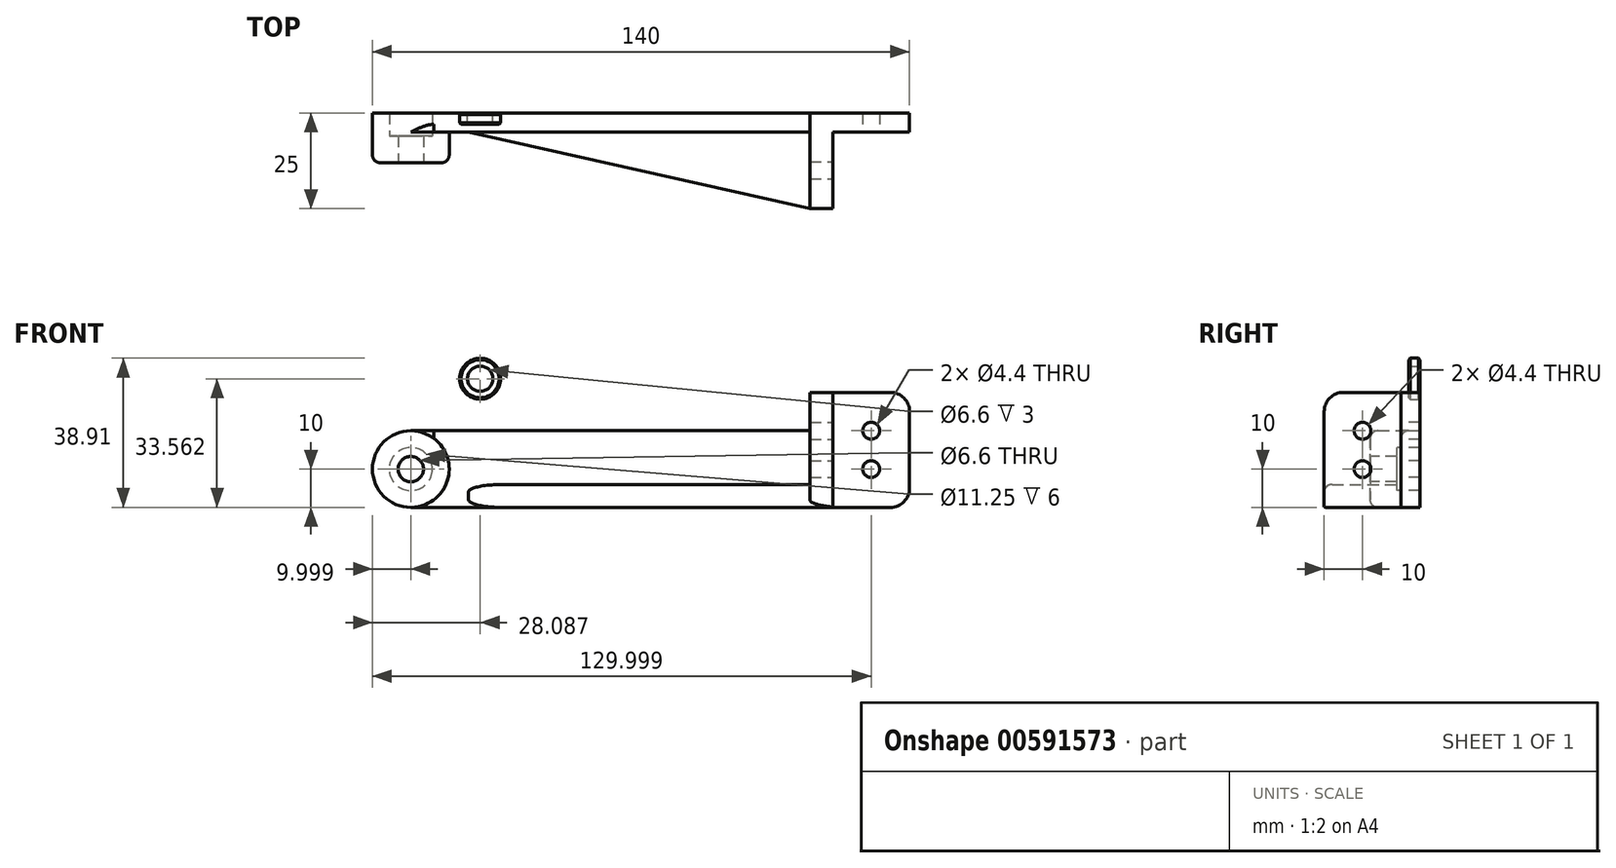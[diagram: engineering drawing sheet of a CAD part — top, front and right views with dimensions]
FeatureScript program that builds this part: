
annotation { "Feature Type Name" : "Feature", "Feature Type Description" : "" }
export const myFeature = defineFeature(function(context is Context, id is Id, definition is map)
    precondition{}
    {
        {
            var Q0;
            Q0=qCreatedBy(makeId("Top.planeOp"),FACE);
            var sketch = newSketch(context, id + "F0", { "sketchPlane" : qUnion([Q0])});
            skLineSegment(sketch, "E0", {"start": v(-72.15, 0) * mm, "end": v(67.85, 0) * mm});
            skLineSegment(sketch, "E1", {"start": v(47.85, -5) * mm, "end": v(47.85, -25) * mm});
            skLineSegment(sketch, "E2", {"start": v(41.85, -25) * mm, "end": v(-47.15, -5) * mm});
            skLineSegment(sketch, "E3", {"start": v(-72.15, -5) * mm, "end": v(-72.15, 0) * mm});
            skLineSegment(sketch, "E4", {"start": v(-72.15, -5) * mm, "end": v(67.85, -5) * mm});
            skLineSegment(sketch, "E5", {"start": v(41.85, -5) * mm, "end": v(41.85, -25) * mm});
            skLineSegment(sketch, "E6", {"start": v(-72.15, -5) * mm, "end": v(-47.15, -5) * mm});
            skLineSegment(sketch, "E7", {"start": v(41.85, -25) * mm, "end": v(47.85, -25) * mm});
            skLineSegment(sketch, "E8", {"start": v(67.85, -5) * mm, "end": v(67.85, 0) * mm});
            skSolve(sketch);
        }
        {
            var Q0;
            {var subQ4=sQuery(id+"F0.wireOp",EDGE,"E4");Q0=makeQuery(id+"F0.imprint","IMPRINT",FACE,{"disambiguationData":[TD([[makeQuery(id+"F0.imprint","IMPRINT",EDGE,{"derivedFrom":subQ4}),-1.0]])]});}
            extrude(context, id + "F1", {"entities" : qUnion([Q0]), "depth" : 6 * mm, "offsetDistance" : 25 * mm});
        }
        {
            var Q0;
            {var subQ4=sQuery(id+"F0.wireOp",EDGE,"E0");Q0=makeQuery(id+"F0.imprint","IMPRINT",FACE,{"disambiguationData":[TD([[makeQuery(id+"F0.imprint","IMPRINT",EDGE,{"derivedFrom":subQ4}),-1.0]])]});}
            var Q1;
            {var subQ0=sQuery(id+"F0.wireOp",EDGE,"E1");Q1=makeQuery(id+"F0.imprint","IMPRINT",FACE,{"disambiguationData":[TD([[makeQuery(id+"F0.imprint","IMPRINT",EDGE,{"derivedFrom":subQ0}),-1.0]])]});}
            extrude(context, id + "F2", {"entities" : qUnion([Q0, Q1]), "operationType" : NewBodyOperationType.ADD, "depth" : 20 * mm, "offsetDistance" : 25 * mm});
        }
        {
            var Q0;
            Q0=makeQuery(id+"F2.opExtrude","CAP_EDGE",EDGE,{"disambiguationData":[OSD([sQuery(id+"F0.wireOp",EDGE,"E3")])],"isStart":false});
            var Q1;
            Q1=makeQuery(id+"F2.opExtrude","CAP_EDGE",EDGE,{"disambiguationData":[OSD([sQuery(id+"F0.wireOp",EDGE,"E3")])],"isStart":true});
            fillet(context, id + "F3", {"entities" : qUnion([Q0, Q1]), "radius" : 10 * mm, "tangentPropagation" : true, "allowEdgeOverflow" : false});
        }
        {
            var Q0;
            Q0=makeQuery(id+"F2.opExtrude","SWEPT_FACE",FACE,{"disambiguationData":[OSD([sQuery(id+"F0.wireOp",EDGE,"E4"),sQuery(id+"F0.wireOp",EDGE,"E6")])]});
            var sketch = newSketch(context, id + "F4", { "sketchPlane" : qUnion([Q0])});
            skCircle(sketch, "E9", {"center": v(-62.15, 10) * mm, "radius": 10 * mm});
            skSolve(sketch);
        }
        {
            var Q0;
            {var subQ0=sQuery(id+"F4.wireOp",EDGE,"E9");var subQ1=sQuery(id+"F0.wireOp",EDGE,"E6");var subQ2=sQuery(id+"F0.wireOp",EDGE,"E4");var subQ3=makeQuery(id+"F4.imprint","INTERSECT",VERTEX,{"derivedFrom":[makeQuery(id+"F2.opExtrude","CAP_EDGE",EDGE,{"disambiguationData":[OSD([subQ2,subQ1])],"isStart":true}),subQ0]});Q0=makeQuery(id+"F4.imprint","IMPRINT",FACE,{"disambiguationData":[TD([[makeQuery(id+"F4.imprint","IMPRINT",EDGE,{"disambiguationData":[TD([[subQ3,-1.0]])],"derivedFrom":subQ0}),1.0]])]});}
            extrude(context, id + "F5", {"entities" : qUnion([Q0]), "operationType" : NewBodyOperationType.ADD, "depth" : 8 * mm, "offsetDistance" : 25 * mm});
        }
        {
            var Q0;
            Q0=makeQuery(id+"F2.opExtrude","CAP_FACE",FACE,{"disambiguationData":[OSD([sQuery(id+"F0.wireOp",EDGE,"E0"),sQuery(id+"F0.wireOp",EDGE,"E1"),sQuery(id+"F0.wireOp",EDGE,"E3"),sQuery(id+"F0.wireOp",EDGE,"E4"),sQuery(id+"F0.wireOp",EDGE,"E5"),sQuery(id+"F0.wireOp",EDGE,"E6"),sQuery(id+"F0.wireOp",EDGE,"E7"),sQuery(id+"F0.wireOp",EDGE,"E8")])],"isStart":false});
            var sketch = newSketch(context, id + "F6", { "sketchPlane" : qUnion([Q0])});
            skLineSegment(sketch, "E10", {"start": v(41.85, -5) * mm, "end": v(41.85, 0) * mm});
            skLineSegment(sketch, "E11", {"start": v(41.85, 0) * mm, "end": v(67.85, 0) * mm});
            skLineSegment(sketch, "E12", {"start": v(67.85, 0) * mm, "end": v(67.85, -5) * mm});
            skLineSegment(sketch, "E13", {"start": v(67.85, -5) * mm, "end": v(47.85, -5) * mm});
            skLineSegment(sketch, "E14", {"start": v(47.85, -5) * mm, "end": v(47.85, -25) * mm});
            skLineSegment(sketch, "E15", {"start": v(47.85, -25) * mm, "end": v(41.85, -25) * mm});
            skLineSegment(sketch, "E16", {"start": v(41.85, -25) * mm, "end": v(41.85, -5) * mm});
            skSolve(sketch);
        }
        {
            var Q0;
            Q0=makeQuery(id+"F6.imprint","IMPRINT",FACE,{"disambiguationData":[TD([[makeQuery(id+"F6.imprint","IMPRINT",EDGE,{"derivedFrom":sQuery(id+"F6.wireOp",EDGE,"E10")}),-1.0]])]});
            extrude(context, id + "F7", {"entities" : qUnion([Q0]), "operationType" : NewBodyOperationType.ADD, "depth" : 10 * mm, "offsetDistance" : 25 * mm});
        }
        {
            var Q0;
            Q0=makeQuery(id+"F2.opExtrude","SWEPT_FACE",FACE,{"disambiguationData":[OSD([sQuery(id+"F0.wireOp",EDGE,"E0")])]});
            var sketch = newSketch(context, id + "F8", { "sketchPlane" : qUnion([Q0])});
            skPoint(sketch, "E17", {"position": v(62.15, 10) * mm});
            skPoint(sketch, "E18", {"position": v(-57.85, 10) * mm});
            skPoint(sketch, "E19", {"position": v(-57.85, 20) * mm});
            skSolve(sketch);
        }
        {
            var Q0;
            Q0=makeQuery(id+"F7.boolean.opBoolean","MERGE",FACE,{"derivedFrom":[makeQuery(id+"F2.opExtrude","SWEPT_FACE",FACE,{"disambiguationData":[OSD([sQuery(id+"F0.wireOp",EDGE,"E5")])]}),makeQuery(id+"F7.opExtrude","SWEPT_FACE",FACE,{"disambiguationData":[OSD([sQuery(id+"F6.wireOp",EDGE,"E10"),sQuery(id+"F6.wireOp",EDGE,"E16")])]})]});
            var sketch = newSketch(context, id + "F9", { "sketchPlane" : qUnion([Q0])});
            skPoint(sketch, "E20", {"position": v(15, 10) * mm});
            skPoint(sketch, "E21", {"position": v(15, 20) * mm});
            skSolve(sketch);
        }
        {
            var Q0;
            Q0=sQuery(id+"F9.wireOp",VERTEX,"E20");
            var Q1;
            Q1=sQuery(id+"F8.wireOp",VERTEX,"E18");
            var Q2;
            Q2=sQuery(id+"F9.wireOp",VERTEX,"E21");
            var Q3;
            Q3=sQuery(id+"F8.wireOp",VERTEX,"E19");
            var Q4;
            Q4=makeQuery(id+"F1.opExtrude","SWEPT_BODY",BODY,{"disambiguationData":[OSD([sQuery(id+"F0.wireOp",EDGE,"E2"),sQuery(id+"F0.wireOp",EDGE,"E4"),sQuery(id+"F0.wireOp",EDGE,"E5")])]});
            hole(context, id + "F10", {"style" : HoleStyle.SIMPLE, "endStyle" : HoleEndStyle.BLIND, "standardTappedOrClearance" : lookupTablePath({ "standard" : "ISO", "fit" : "Normal", "size" : "M4", "type" : "Clearance" }), "standardBlindInLast" : lookupTablePath({ "fit" : "Standard", "standard" : "ISO", "size" : "M4", "type" : "Clearance" }), "holeDiameter" : 4.4 * mm, "majorDiameter" : 5 * mm, "holeDepth" : 10 * mm, "isTappedThrough" : true, "tappedDepth" : 12 * mm, "tapClearance" : 3, "locations" : qUnion([Q0, Q1, Q2, Q3]), "scope" : qUnion([Q4])});
        }
        {
            var Q0;
            Q0=sQuery(id+"F8.wireOp",VERTEX,"E17");
            var Q1;
            Q1=makeQuery(id+"F1.opExtrude","SWEPT_BODY",BODY,{"disambiguationData":[OSD([sQuery(id+"F0.wireOp",EDGE,"E2"),sQuery(id+"F0.wireOp",EDGE,"E4"),sQuery(id+"F0.wireOp",EDGE,"E5")])]});
            hole(context, id + "F11", {"style" : HoleStyle.C_BORE, "endStyle" : HoleEndStyle.THROUGH, "standardTappedOrClearance" : lookupTablePath({ "standard" : "ISO", "fit" : "Normal", "size" : "M6", "type" : "Clearance" }), "standardBlindInLast" : lookupTablePath({ "fit" : "Standard", "standard" : "ISO", "size" : "M6", "type" : "Clearance" }), "holeDiameter" : 6.6 * mm, "cBoreDiameter" : 11.25 * mm, "cBoreDepth" : 6 * mm, "majorDiameter" : 5 * mm, "isTappedThrough" : true, "tappedDepth" : 12 * mm, "tapClearance" : 3, "locations" : qUnion([Q0]), "scope" : qUnion([Q1])});
        }
        {
            var Q0;
            Q0=makeQuery(id+"F5.opExtrude","CAP_EDGE",EDGE,{"disambiguationData":[OSD([sQuery(id+"F4.wireOp",EDGE,"E9")])],"isStart":false});
            var Q1;
            Q1=makeQuery(id+"F2.opExtrude","CAP_EDGE",EDGE,{"disambiguationData":[OSD([sQuery(id+"F0.wireOp",EDGE,"E4"),sQuery(id+"F0.wireOp",EDGE,"E6")])],"isStart":false});
            var Q2;
            Q2=makeQuery(id+"F1.opExtrude","CAP_EDGE",EDGE,{"disambiguationData":[OSD([sQuery(id+"F0.wireOp",EDGE,"E2")])],"isStart":true});
            var Q3;
            Q3=makeQuery(id+"F1.opExtrude","CAP_EDGE",EDGE,{"disambiguationData":[OSD([sQuery(id+"F0.wireOp",EDGE,"E2")])],"isStart":false});
            var Q4;
            Q4=makeQuery(id+"F2.opExtrude","CAP_EDGE",EDGE,{"disambiguationData":[OSD([sQuery(id+"F0.wireOp",EDGE,"E5")])],"isStart":false});
            fillet(context, id + "F12", {"entities" : qUnion([Q0, Q1, Q2, Q3, Q4]), "radius" : 2 * mm, "tangentPropagation" : true, "allowEdgeOverflow" : false});
        }
        {
            var Q0;
            Q0=makeQuery(id+"F7.opExtrude","CAP_EDGE",EDGE,{"disambiguationData":[OSD([sQuery(id+"F6.wireOp",EDGE,"E12")])],"isStart":false});
            var Q1;
            Q1=makeQuery(id+"F7.opExtrude","CAP_EDGE",EDGE,{"disambiguationData":[OSD([sQuery(id+"F6.wireOp",EDGE,"E15")])],"isStart":false});
            var Q2;
            Q2=makeQuery(id+"F2.opExtrude","CAP_EDGE",EDGE,{"disambiguationData":[OSD([sQuery(id+"F0.wireOp",EDGE,"E8")])],"isStart":true});
            var Q3;
            Q3=makeQuery(id+"F7.opExtrude","CAP_EDGE",EDGE,{"disambiguationData":[OSD([sQuery(id+"F6.wireOp",EDGE,"E10"),sQuery(id+"F6.wireOp",EDGE,"E16")])],"isStart":true});
            fillet(context, id + "F13", {"entities" : qUnion([Q0, Q1, Q2, Q3]), "radius" : 5 * mm, "tangentPropagation" : true, "allowEdgeOverflow" : false});
        }
        {
            var Q0;
            Q0=qCreatedBy(makeId("Front.planeOp"),FACE);
            var sketch = newSketch(context, id + "F14", { "sketchPlane" : qUnion([Q0])});
            skCircle(sketch, "E22", {"center": v(-44.06, 33.56) * mm, "radius": 5.35 * mm});
            skCircle(sketch, "E23", {"center": v(-44.06, 33.56) * mm, "radius": 3.3 * mm});
            skSolve(sketch);
        }
        {
            var Q0;
            Q0 = qSketchRegion(id + "F14", true);
            extrude(context, id + "F15", {"entities" : qUnion([Q0]), "depth" : 3 * mm, "offsetDistance" : 25 * mm});
        }
        {
            var Q0;
            Q0=makeQuery(id+"F15.opExtrude","CAP_EDGE",EDGE,{"disambiguationData":[OSD([sQuery(id+"F14.wireOp",EDGE,"E22")])],"isStart":false});
            var Q1;
            Q1=makeQuery(id+"F15.opExtrude","CAP_EDGE",EDGE,{"disambiguationData":[OSD([sQuery(id+"F14.wireOp",EDGE,"E22")])],"isStart":true});
            chamfer(context, id + "F16", {"entities" : qUnion([Q0, Q1]), "width" : .4 * mm, "tangentPropagation" : true});
        }
    });
